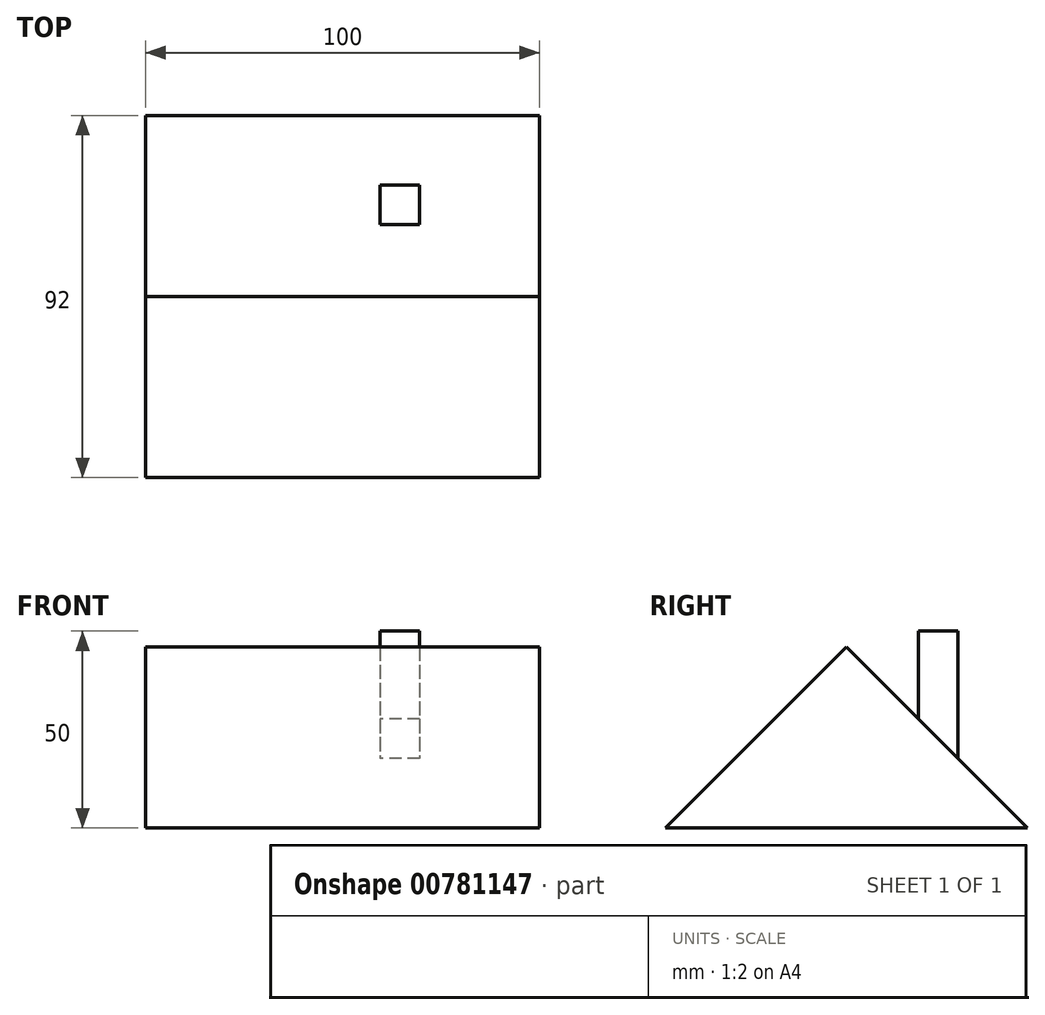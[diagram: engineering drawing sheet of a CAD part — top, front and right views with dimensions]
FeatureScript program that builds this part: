
annotation { "Feature Type Name" : "Feature", "Feature Type Description" : "" }
export const myFeature = defineFeature(function(context is Context, id is Id, definition is map)
    precondition{}
    {
        {
            var Q0;
            Q0=qCreatedBy(makeId("Top.planeOp"),FACE);
            var sketch = newSketch(context, id + "F0", { "sketchPlane" : qUnion([Q0])});
            skLineSegment(sketch, "E0.bottom", {"start": v(-59.55, 67.13) * mm, "end": v(40.45, 67.13) * mm});
            skLineSegment(sketch, "E0.top", {"start": v(-59.55, -24.87) * mm, "end": v(40.45, -24.87) * mm});
            skLineSegment(sketch, "E0.left", {"start": v(-59.55, 67.13) * mm, "end": v(-59.55, -24.87) * mm});
            skLineSegment(sketch, "E0.right", {"start": v(40.45, 67.13) * mm, "end": v(40.45, -24.87) * mm});
            skSolve(sketch);
        }
        {
            var Q0;
            Q0=makeQuery(id+"F0.imprint","IMPRINT",FACE,{"disambiguationData":[TD([[makeQuery(id+"F0.imprint","IMPRINT",EDGE,{"derivedFrom":sQuery(id+"F0.wireOp",EDGE,"E0.bottom")}),-1.0]])]});
            var sketch = newSketch(context, id + "F1", { "sketchPlane" : qUnion([Q0])});
            skLineSegment(sketch, "E1.bottom", {"start": v(0, 49.45) * mm, "end": v(10, 49.45) * mm});
            skLineSegment(sketch, "E1.top", {"start": v(0, 39.45) * mm, "end": v(10, 39.45) * mm});
            skLineSegment(sketch, "E1.left", {"start": v(0, 49.45) * mm, "end": v(0, 39.45) * mm});
            skLineSegment(sketch, "E1.right", {"start": v(10, 49.45) * mm, "end": v(10, 39.45) * mm});
            skSolve(sketch);
        }
        {
            var Q0;
            Q0 = qSketchRegion(id + "F1", true);
            extrude(context, id + "F2", {"entities" : qUnion([Q0]), "depth" : 50 * mm, "offsetDistance" : 25 * mm});
        }
        {
            var Q0;
            Q0 = qSketchRegion(id + "F0", true);
            extrude(context, id + "F3", {"entities" : qUnion([Q0]), "operationType" : NewBodyOperationType.ADD, "depth" : 46 * mm, "offsetDistance" : 25 * mm});
        }
        {
            var Q0;
            Q0=makeQuery(id+"F3.opExtrude","CAP_EDGE",EDGE,{"disambiguationData":[OSD([sQuery(id+"F0.wireOp",EDGE,"E0.top")])],"isStart":false});
            var Q1;
            Q1=makeQuery(id+"F3.opExtrude","CAP_EDGE",EDGE,{"disambiguationData":[OSD([sQuery(id+"F0.wireOp",EDGE,"E0.bottom")])],"isStart":false});
            chamfer(context, id + "F4", {"entities" : qUnion([Q0, Q1]), "width" : 46 * mm, "tangentPropagation" : true});
        }
    });
